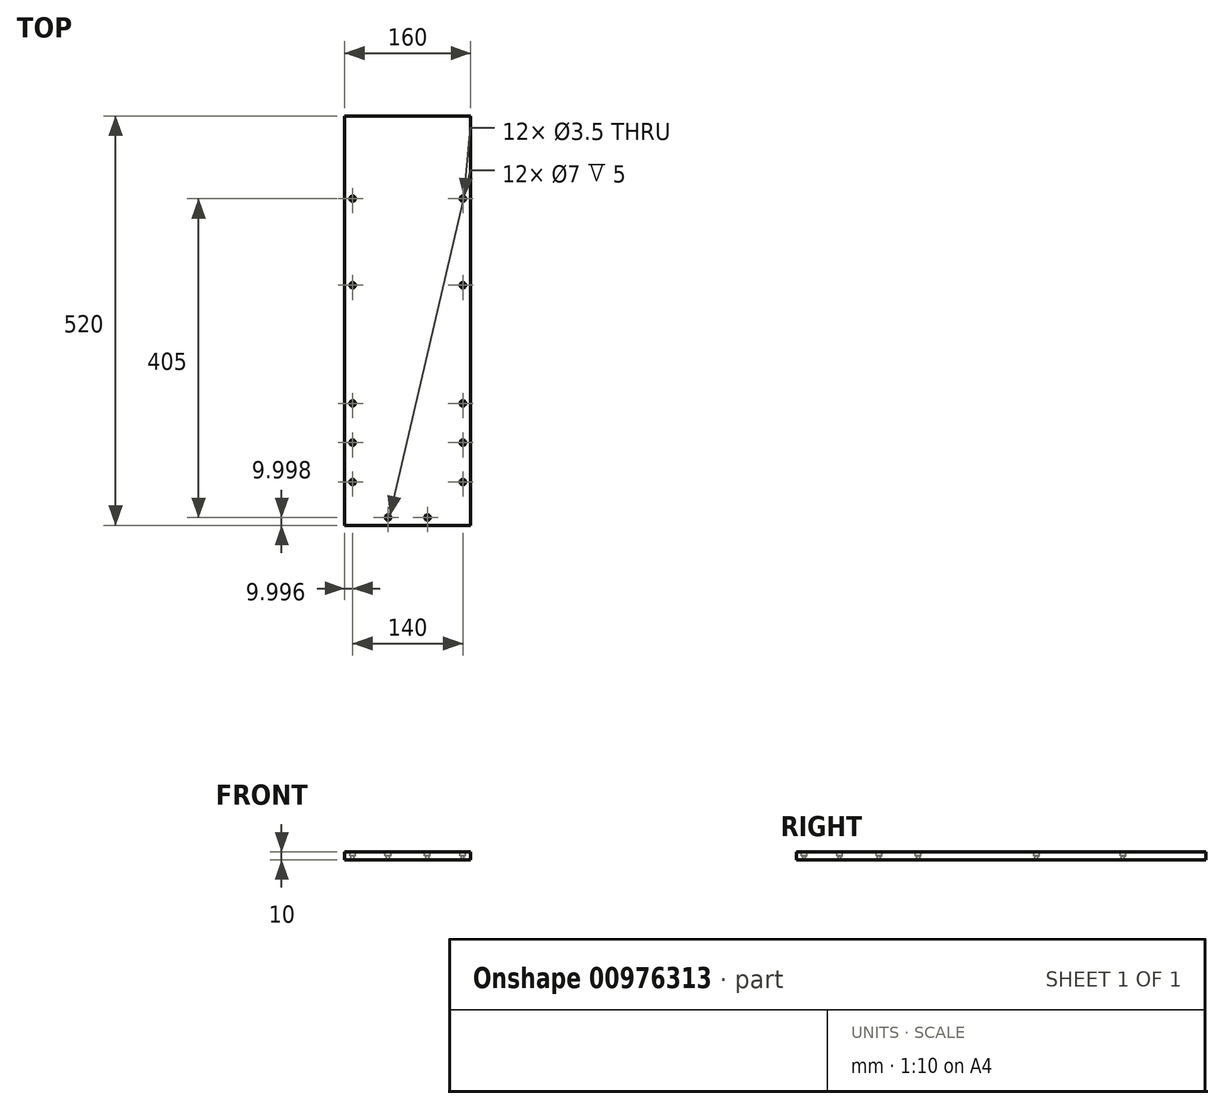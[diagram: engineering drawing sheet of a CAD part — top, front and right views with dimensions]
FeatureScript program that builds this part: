
annotation { "Feature Type Name" : "Feature", "Feature Type Description" : "" }
export const myFeature = defineFeature(function(context is Context, id is Id, definition is map)
    precondition{}
    {
        {
            var Q0;
            Q0=qCreatedBy(makeId("Top.planeOp"),FACE);
            var sketch = newSketch(context, id + "F0", { "sketchPlane" : qUnion([Q0])});
            skLineSegment(sketch, "E0.bottom", {"start": v(-101.03, 393.3) * mm, "end": v(58.97, 393.3) * mm});
            skLineSegment(sketch, "E0.top", {"start": v(-101.03, -126.7) * mm, "end": v(58.97, -126.7) * mm});
            skLineSegment(sketch, "E0.left", {"start": v(-101.03, 393.3) * mm, "end": v(-101.03, -126.7) * mm});
            skLineSegment(sketch, "E0.right", {"start": v(58.97, 393.3) * mm, "end": v(58.97, -126.7) * mm});
            skLineSegment(sketch, "E1.bottom", {"start": v(-96.03, 388.3) * mm, "end": v(53.97, 388.3) * mm});
            skLineSegment(sketch, "E1.top", {"start": v(-96.03, -121.7) * mm, "end": v(53.97, -121.7) * mm});
            skLineSegment(sketch, "E1.left", {"start": v(-96.03, 388.3) * mm, "end": v(-96.03, -121.7) * mm});
            skLineSegment(sketch, "E1.right", {"start": v(53.97, 388.3) * mm, "end": v(53.97, -121.7) * mm});
            skSolve(sketch);
        }
        {
            var Q0;
            Q0=makeQuery(id+"F0.imprint","IMPRINT",FACE,{"disambiguationData":[TD([[makeQuery(id+"F0.imprint","IMPRINT",EDGE,{"derivedFrom":sQuery(id+"F0.wireOp",EDGE,"E0.bottom")}),-1.0]])]});
            var Q1;
            Q1=makeQuery(id+"F0.imprint","IMPRINT",FACE,{"disambiguationData":[TD([[makeQuery(id+"F0.imprint","IMPRINT",EDGE,{"derivedFrom":sQuery(id+"F0.wireOp",EDGE,"E1.bottom")}),-1.0]])]});
            extrude(context, id + "F1", {"entities" : qUnion([Q0, Q1]), "depth" : 10 * mm, "offsetDistance" : 25 * mm});
        }
        {
            var Q0;
            Q0=makeQuery(id+"F1.opExtrude","CAP_FACE",FACE,{"disambiguationData":[OSD([sQuery(id+"F0.wireOp",EDGE,"E0.bottom"),sQuery(id+"F0.wireOp",EDGE,"E0.top"),sQuery(id+"F0.wireOp",EDGE,"E0.left"),sQuery(id+"F0.wireOp",EDGE,"E0.right")])],"isStart":false});
            var sketch = newSketch(context, id + "F2", { "sketchPlane" : qUnion([Q0])});
            skCircle(sketch, "E2", {"center": v(-91.03, 288.3) * mm, "radius": 2.5 * mm});
            skCircle(sketch, "E3", {"center": v(-91.03, 178.3) * mm, "radius": 2.5 * mm});
            skCircle(sketch, "E4", {"center": v(-91.03, 28.3) * mm, "radius": 2.5 * mm});
            skCircle(sketch, "E5", {"center": v(-91.03, -21.7) * mm, "radius": 2.5 * mm});
            skCircle(sketch, "E6", {"center": v(-91.03, -71.7) * mm, "radius": 2.5 * mm});
            skCircle(sketch, "E7", {"center": v(48.97, 288.3) * mm, "radius": 2.5 * mm});
            skCircle(sketch, "E8", {"center": v(48.97, 178.3) * mm, "radius": 2.5 * mm});
            skCircle(sketch, "E9", {"center": v(-46.03, -116.7) * mm, "radius": 2.5 * mm});
            skCircle(sketch, "E10", {"center": v(3.97, -116.7) * mm, "radius": 2.5 * mm});
            skCircle(sketch, "E11", {"center": v(48.97, 28.3) * mm, "radius": 2.5 * mm});
            skCircle(sketch, "E12", {"center": v(48.97, -21.7) * mm, "radius": 2.5 * mm});
            skCircle(sketch, "E13", {"center": v(48.97, -71.7) * mm, "radius": 2.5 * mm});
            skSolve(sketch);
        }
        {
            var Q0;
            Q0=sQuery(id+"F2.wireOp",VERTEX,"E2.center");
            var Q1;
            Q1=sQuery(id+"F2.wireOp",VERTEX,"E3.center");
            var Q2;
            Q2=sQuery(id+"F2.wireOp",VERTEX,"E8.center");
            var Q3;
            Q3=sQuery(id+"F2.wireOp",VERTEX,"E7.center");
            var Q4;
            Q4=sQuery(id+"F2.wireOp",VERTEX,"E11.center");
            var Q5;
            Q5=sQuery(id+"F2.wireOp",VERTEX,"E12.center");
            var Q6;
            Q6=sQuery(id+"F2.wireOp",VERTEX,"E13.center");
            var Q7;
            Q7=sQuery(id+"F2.wireOp",VERTEX,"E10.center");
            var Q8;
            Q8=sQuery(id+"F2.wireOp",VERTEX,"E9.center");
            var Q9;
            Q9=sQuery(id+"F2.wireOp",VERTEX,"E6.center");
            var Q10;
            Q10=sQuery(id+"F2.wireOp",VERTEX,"E5.center");
            var Q11;
            Q11=sQuery(id+"F2.wireOp",VERTEX,"E4.center");
            var Q12;
            Q12=makeQuery(id+"F1.opExtrude","SWEPT_BODY",BODY,{"disambiguationData":[OSD([sQuery(id+"F0.wireOp",EDGE,"E0.bottom"),sQuery(id+"F0.wireOp",EDGE,"E0.top"),sQuery(id+"F0.wireOp",EDGE,"E0.left"),sQuery(id+"F0.wireOp",EDGE,"E0.right")])]});
            hole(context, id + "F3", {"style" : HoleStyle.C_BORE, "endStyle" : HoleEndStyle.THROUGH, "holeDiameter" : 3.5 * mm, "cBoreDiameter" : 7 * mm, "cBoreDepth" : 5 * mm, "majorDiameter" : 5 * mm, "isTappedThrough" : true, "tappedDepth" : 19.25 * mm, "tapClearance" : 3, "locations" : qUnion([Q0, Q1, Q2, Q3, Q4, Q5, Q6, Q7, Q8, Q9, Q10, Q11]), "scope" : qUnion([Q12])});
        }
    });
